# Revit family: Seating-Side_Stool_Chair-Teknion-Zones_ZNMDZ-R2013
name_source: partatom
category: Furniture
revit_build: Autodesk Revit Architecture 2013 (Build: 20130531_2115(x64)
units: mm (PartAtom-declared; Revit-internal decimal feet)

## types (2) — shared parameters
Assembly Code = E2020200
Back Leg Support End = 1 15/32"
Back Leg Support Start = 0"
Depth = 23 3/8"
Manufacturer = Teknion
Manufacturer Fax = 416.661.4586
Part Number = ZNMDZ
Product Documentation Link = http://www.teknion.com
Product Line = Zones
Product Page URL = http://www.teknion.com
Series = Zones
Sustainability Data = http://www.teknion.com
URL = www.teknion.com
Warranty = http://www.teknion.com
Width = 20 3/8"

## per-type parameters (varying)
| type | Description | Footrest Height | Front Leg Offset Horizontal | Front Leg Offset Vertical | Height | Legs Bar Height | Legs Counter Height | Model | Seat Height |
| Bar Seat Height | Zones Side Stool, 4-Wood Legs, No Arms, Plastic Back, Bar Height | 13 5/8" | 11/32" | 0" | 30 3/4" | Yes | No | ZNMDZB | 30 3/4" |
| Counter Height | Zones Side Stool, 4-Wood Legs, No Arms, Plastic Back, Counter Height | 7 11/16" | 29/32" | 25/32" | 24 3/4" | No | Yes | ZNMDZC | 24 3/4" |

## geometry (parser evidence)
native form markers: Blend x68, Sweep x7
no freeform markers — native parametric forms only
